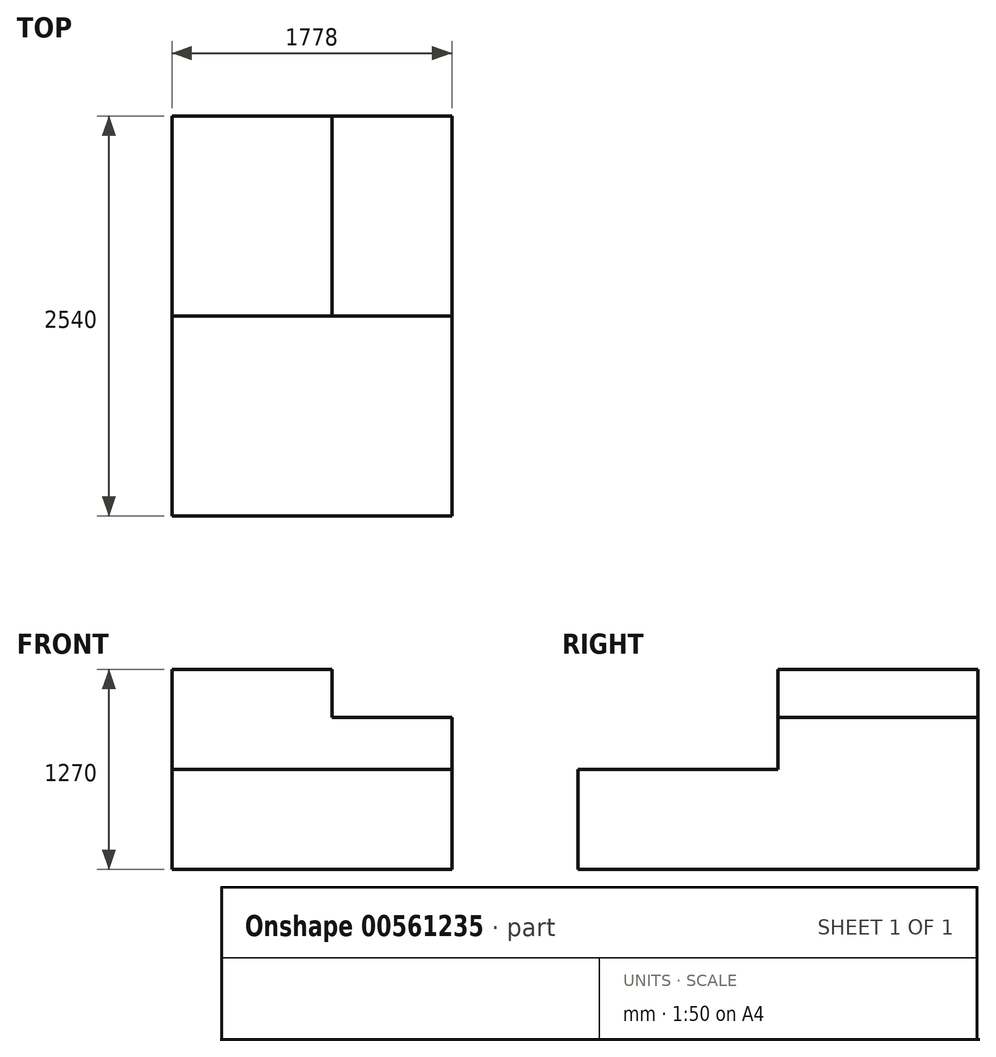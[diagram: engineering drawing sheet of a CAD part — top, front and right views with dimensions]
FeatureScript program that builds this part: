
annotation { "Feature Type Name" : "Feature", "Feature Type Description" : "" }
export const myFeature = defineFeature(function(context is Context, id is Id, definition is map)
    precondition{}
    {
        {
            var Q0;
            Q0=qCreatedBy(makeId("Top.planeOp"),FACE);
            var sketch = newSketch(context, id + "F0", { "sketchPlane" : qUnion([Q0])});
            skLineSegment(sketch, "E0", {"start": v(-659, -219.52) * mm, "end": v(1119, -219.52) * mm});
            skLineSegment(sketch, "E1", {"start": v(1119, -219.52) * mm, "end": v(1119, 1050.48) * mm});
            skLineSegment(sketch, "E2", {"start": v(1119, 1050.48) * mm, "end": v(-659, 1050.48) * mm});
            skLineSegment(sketch, "E3", {"start": v(-659, 1050.48) * mm, "end": v(-659, -219.52) * mm});
            skLineSegment(sketch, "E4", {"start": v(1119, 1050.48) * mm, "end": v(1119, 2320.48) * mm});
            skLineSegment(sketch, "E5", {"start": v(1119, 2320.48) * mm, "end": v(357, 2320.48) * mm});
            skLineSegment(sketch, "E6", {"start": v(357, 2320.48) * mm, "end": v(357, 1050.48) * mm});
            skLineSegment(sketch, "E7", {"start": v(357, 1050.48) * mm, "end": v(1119, 1050.48) * mm});
            skLineSegment(sketch, "E8", {"start": v(357, 2320.48) * mm, "end": v(-659, 2320.48) * mm});
            skLineSegment(sketch, "E9", {"start": v(357, 1050.48) * mm, "end": v(-659, 1050.48) * mm});
            skLineSegment(sketch, "E10", {"start": v(-659, 2320.48) * mm, "end": v(-659, 1050.48) * mm});
            skSolve(sketch);
        }
        {
            var Q0;
            Q0 = qSketchRegion(id + "F0", true);
            extrude(context, id + "F1", {"entities" : qUnion([Q0]), "depth" : 635 * mm, "offsetDistance" : 25.4 * mm});
        }
        {
            var Q0;
            Q0=makeQuery(id+"F1.opExtrude","CAP_FACE",FACE,{"disambiguationData":[OSD([sQuery(id+"F0.wireOp",EDGE,"E0"),sQuery(id+"F0.wireOp",EDGE,"E1"),sQuery(id+"F0.wireOp",EDGE,"E3"),sQuery(id+"F0.wireOp",EDGE,"E4"),sQuery(id+"F0.wireOp",EDGE,"E5"),sQuery(id+"F0.wireOp",EDGE,"E8"),sQuery(id+"F0.wireOp",EDGE,"E10")])],"isStart":false});
            var sketch = newSketch(context, id + "F2", { "sketchPlane" : qUnion([Q0])});
            skLineSegment(sketch, "E11", {"start": v(1119, 2320.48) * mm, "end": v(357, 2320.48) * mm});
            skLineSegment(sketch, "E12", {"start": v(357, 2320.48) * mm, "end": v(357, 1050.48) * mm});
            skLineSegment(sketch, "E13", {"start": v(357, 1050.48) * mm, "end": v(1119, 1050.48) * mm});
            skLineSegment(sketch, "E14", {"start": v(1119, 1050.48) * mm, "end": v(1119, 2320.48) * mm});
            skSolve(sketch);
        }
        {
            var Q0;
            Q0 = qSketchRegion(id + "F2", true);
            extrude(context, id + "F3", {"entities" : qUnion([Q0]), "operationType" : NewBodyOperationType.ADD, "depth" : 330.2 * mm, "offsetDistance" : 25.4 * mm});
        }
        {
            var Q0;
            Q0=makeQuery(id+"F1.opExtrude","CAP_FACE",FACE,{"disambiguationData":[OSD([sQuery(id+"F0.wireOp",EDGE,"E0"),sQuery(id+"F0.wireOp",EDGE,"E1"),sQuery(id+"F0.wireOp",EDGE,"E3"),sQuery(id+"F0.wireOp",EDGE,"E4"),sQuery(id+"F0.wireOp",EDGE,"E5"),sQuery(id+"F0.wireOp",EDGE,"E8"),sQuery(id+"F0.wireOp",EDGE,"E10")])],"isStart":false});
            var sketch = newSketch(context, id + "F4", { "sketchPlane" : qUnion([Q0])});
            skLineSegment(sketch, "E15", {"start": v(357, 2320.48) * mm, "end": v(357, 1050.48) * mm});
            skLineSegment(sketch, "E16", {"start": v(357, 1050.48) * mm, "end": v(-659, 1050.48) * mm});
            skLineSegment(sketch, "E17", {"start": v(-659, 1050.48) * mm, "end": v(-659, 2320.48) * mm});
            skLineSegment(sketch, "E18", {"start": v(-659, 2320.48) * mm, "end": v(357, 2320.48) * mm});
            skSolve(sketch);
        }
        {
            var Q0;
            Q0 = qSketchRegion(id + "F4", true);
            extrude(context, id + "F5", {"entities" : qUnion([Q0]), "operationType" : NewBodyOperationType.ADD, "depth" : 635 * mm, "offsetDistance" : 25.4 * mm});
        }
    });
